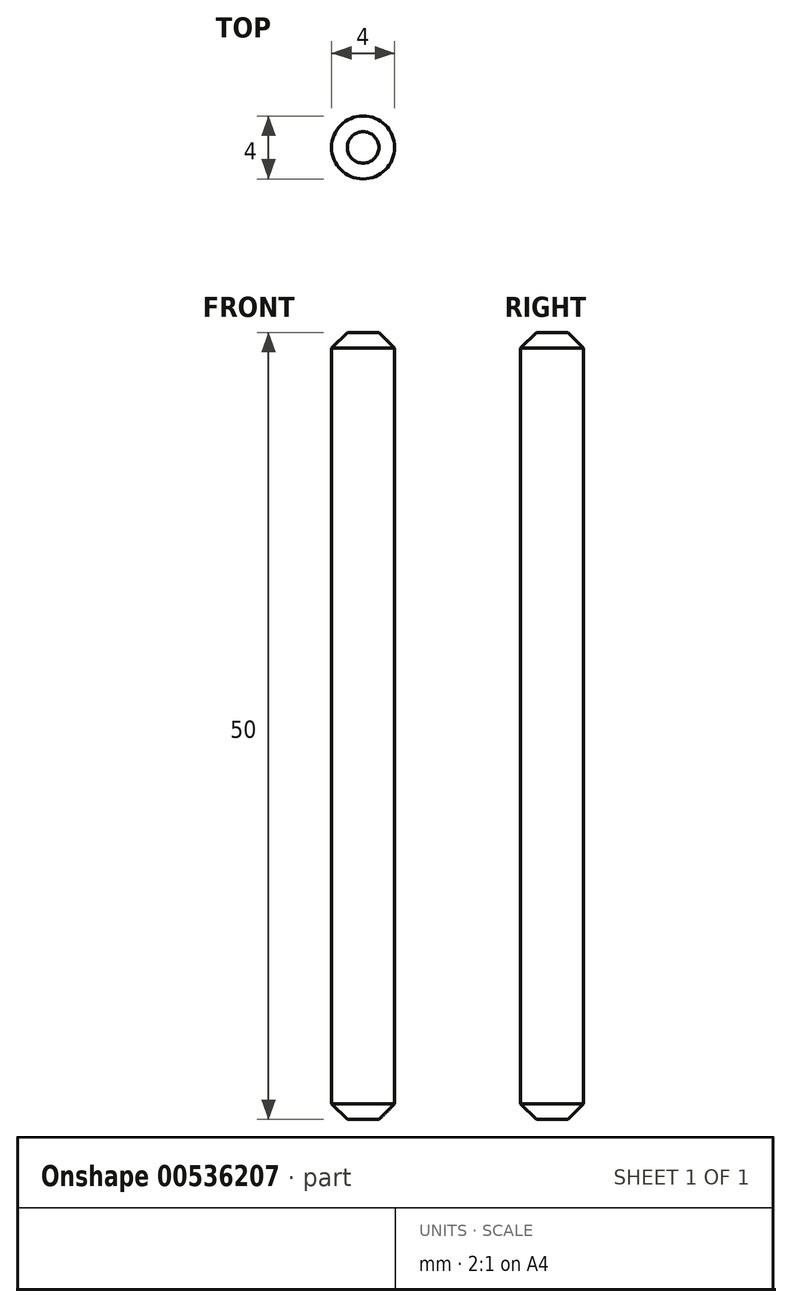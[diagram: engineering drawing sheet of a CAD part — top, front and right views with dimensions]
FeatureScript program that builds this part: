
annotation { "Feature Type Name" : "Feature", "Feature Type Description" : "" }
export const myFeature = defineFeature(function(context is Context, id is Id, definition is map)
    precondition{}
    {
        {
            var Q0;
            Q0=qCreatedBy(makeId("Top.planeOp"),FACE);
            var sketch = newSketch(context, id + "F0", { "sketchPlane" : qUnion([Q0])});
            skCircle(sketch, "E0", {"center": v(0, 0) * mm, "radius": 2 * mm});
            skSolve(sketch);
        }
        {
            var Q0;
            Q0=makeQuery(id+"F0.imprint","IMPRINT",FACE,{"disambiguationData":[TD([[makeQuery(id+"F0.imprint","IMPRINT",EDGE,{"derivedFrom":sQuery(id+"F0.wireOp",EDGE,"E0")}),1.0]])]});
            extrude(context, id + "F1", {"entities" : qUnion([Q0]), "depth" : 50 * mm, "offsetDistance" : 25 * mm});
        }
        {
            var Q0;
            Q0=makeQuery(id+"F1.opExtrude","CAP_EDGE",EDGE,{"disambiguationData":[OSD([sQuery(id+"F0.wireOp",EDGE,"E0")])],"isStart":true});
            chamfer(context, id + "F2", {"entities" : qUnion([Q0]), "width" : 1 * mm, "tangentPropagation" : true});
        }
        {
            var Q0;
            Q0=makeQuery(id+"F1.opExtrude","CAP_EDGE",EDGE,{"disambiguationData":[OSD([sQuery(id+"F0.wireOp",EDGE,"E0")])],"isStart":false});
            chamfer(context, id + "F3", {"entities" : qUnion([Q0]), "width" : 1 * mm, "tangentPropagation" : true});
        }
    });
